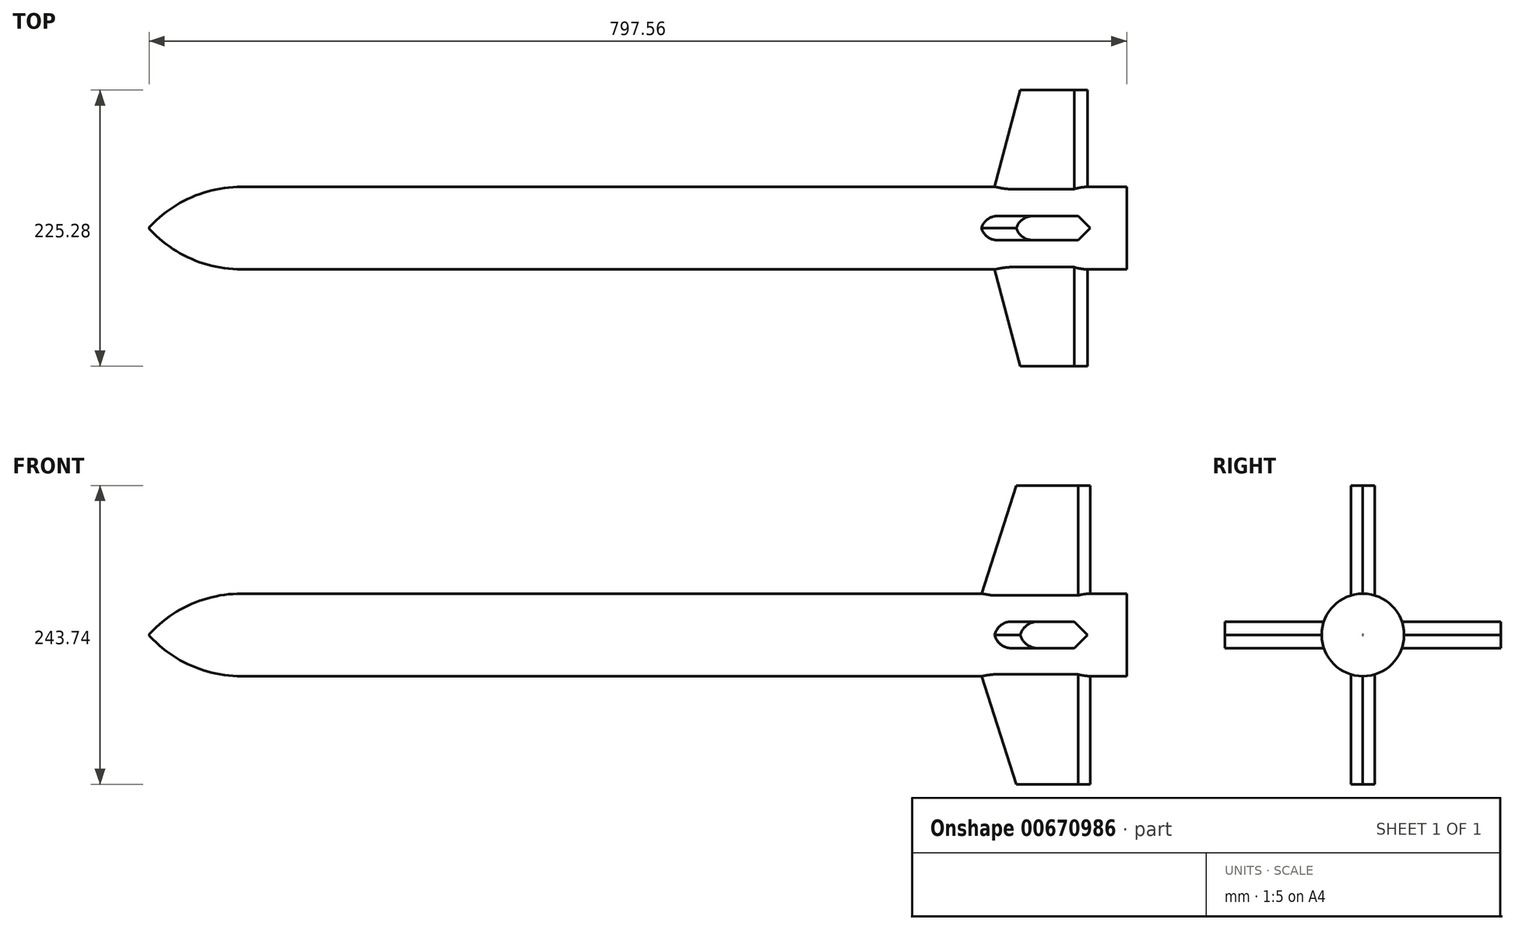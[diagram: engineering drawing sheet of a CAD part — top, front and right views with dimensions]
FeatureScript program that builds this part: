
annotation { "Feature Type Name" : "Feature", "Feature Type Description" : "" }
export const myFeature = defineFeature(function(context is Context, id is Id, definition is map)
    precondition{}
    {
        {
            var Q0;
            Q0=qCreatedBy(makeId("Right.planeOp"),FACE);
            var sketch = newSketch(context, id + "F0", { "sketchPlane" : qUnion([Q0])});
            skCircle(sketch, "E0", {"center": v(0, 0) * mm, "radius": 33.64 * mm});
            skSolve(sketch);
        }
        {
            var Q0;
            Q0 = qSketchRegion(id + "F0", true);
            extrude(context, id + "F1", {"entities" : qUnion([Q0]), "endBound" : BoundingType.SYMMETRIC, "oppositeDirection" : true, "depth" : 797.56 * mm, "offsetDistance" : 25.4 * mm});
        }
        {
            var Q0;
            Q0=makeQuery(id+"F1.opExtrude","CAP_EDGE",EDGE,{"disambiguationData":[OSD([sQuery(id+"F0.wireOp",EDGE,"E0")])],"isStart":false});
            chamfer(context, id + "F2", {"entities" : qUnion([Q0]), "width" : 33.02 * mm, "tangentPropagation" : true});
        }
        {
            var Q0;
            {var subQ0=sQuery(id+"F0.wireOp",EDGE,"E0");Q0=makeQuery(id+"F2.opChamfer","BLEND_EDGE",EDGE,{"blendedFrom":[makeQuery(id+"F1.opExtrude","CAP_EDGE",EDGE,{"disambiguationData":[OSD([subQ0])],"isStart":false}),makeQuery(id+"F1.opExtrude","SWEPT_FACE",FACE,{"disambiguationData":[OSD([subQ0])]})],"blendedInto":[makeQuery(id+"F1.opExtrude","SWEPT_FACE",FACE,{"disambiguationData":[OSD([subQ0])]})]});}
            fillet(context, id + "F3", {"entities" : qUnion([Q0]), "radius" : 101.73 * mm, "tangentPropagation" : true, "allowEdgeOverflow" : false});
        }
        {
            var Q0;
            Q0=qCreatedBy(makeId("Right.planeOp"),FACE);
            var sketch = newSketch(context, id + "F4", { "sketchPlane" : qUnion([Q0])});
            skCircle(sketch, "E1", {"center": v(0, 0) * mm, "radius": 30.05 * mm});
            skCircle(sketch, "E2", {"center": v(0, 0) * mm, "radius": 33.57 * mm});
            skSolve(sketch);
        }
        {
            var Q0;
            Q0=sQuery(id+"F4.wireOp",EDGE,"E1");
            var Q1;
            Q1=sQuery(id+"F4.wireOp",EDGE,"E2");
            extrude(context, id + "F5", {"bodyType" : ToolBodyType.SURFACE, "surfaceEntities" : qUnion([Q0, Q1]), "depth" : 431.8 * mm, "offsetDistance" : 25.4 * mm});
        }
        {
            var Q0;
            Q0=qCreatedBy(makeId("Front.planeOp"),FACE);
            var sketch = newSketch(context, id + "F6", { "sketchPlane" : qUnion([Q0])});
            skLineSegment(sketch, "E3.bottom", {"start": v(374.4, -121.87) * mm, "end": v(308.36, -121.87) * mm});
            skLineSegment(sketch, "E3.top", {"start": v(374.4, 121.87) * mm, "end": v(308.36, 121.87) * mm});
            skLineSegment(sketch, "E3.left", {"start": v(374.4, -121.87) * mm, "end": v(374.4, 121.87) * mm});
            skLineSegment(sketch, "E3.right", {"start": v(308.36, -121.87) * mm, "end": v(308.36, 121.87) * mm});
            skPoint(sketch, "E3.middle", {"position": v(341.38, 0) * mm});
            skLineSegment(sketch, "E4", {"start": v(308.36, 121.87) * mm, "end": v(269.13, 0) * mm});
            skLineSegment(sketch, "E5", {"start": v(269.13, 0) * mm, "end": v(308.36, -121.87) * mm});
            skSolve(sketch);
        }
        {
            var Q0;
            Q0 = qSketchRegion(id + "F6", true);
            extrude(context, id + "F7", {"entities" : qUnion([Q0]), "operationType" : NewBodyOperationType.ADD, "endBound" : BoundingType.SYMMETRIC, "depth" : 19.6 * mm, "offsetDistance" : 25.4 * mm});
        }
        {
            var Q0;
            Q0=makeQuery(id+"F7.opExtrude","CAP_EDGE",EDGE,{"disambiguationData":[OSD([sQuery(id+"F6.wireOp",EDGE,"E5")])],"isStart":false});
            var Q1;
            Q1=makeQuery(id+"F7.opExtrude","CAP_EDGE",EDGE,{"disambiguationData":[OSD([sQuery(id+"F6.wireOp",EDGE,"E5")])],"isStart":true});
            var Q2;
            Q2=makeQuery(id+"F7.opExtrude","CAP_EDGE",EDGE,{"disambiguationData":[OSD([sQuery(id+"F6.wireOp",EDGE,"E4")])],"isStart":false});
            var Q3;
            Q3=makeQuery(id+"F7.opExtrude","CAP_EDGE",EDGE,{"disambiguationData":[OSD([sQuery(id+"F6.wireOp",EDGE,"E4")])],"isStart":true});
            fillet(context, id + "F8", {"entities" : qUnion([Q0, Q1, Q2, Q3]), "radius" : 13.04 * mm, "tangentPropagation" : true, "allowEdgeOverflow" : false});
        }
        {
            var Q0;
            {var subQ0=sQuery(id+"F6.wireOp",EDGE,"E3.left");var subQ1=sQuery(id+"F6.wireOp",EDGE,"E3.bottom");Q0=makeQuery(id+"F7.boolean.opBoolean","SPLIT",EDGE,{"disambiguationData":[TD([makeQuery(id+"F7.opExtrude","SWEPT_FACE",FACE,{"disambiguationData":[OSD([subQ1])]})])],"derivedFrom":makeQuery(id+"F7.opExtrude","CAP_EDGE",EDGE,{"disambiguationData":[OSD([subQ0])],"isStart":false})});}
            var Q1;
            {var subQ0=sQuery(id+"F6.wireOp",EDGE,"E3.bottom");var subQ1=sQuery(id+"F6.wireOp",EDGE,"E3.left");Q1=makeQuery(id+"F7.boolean.opBoolean","SPLIT",EDGE,{"disambiguationData":[TD([makeQuery(id+"F7.opExtrude","SWEPT_FACE",FACE,{"disambiguationData":[OSD([subQ0])]})])],"derivedFrom":makeQuery(id+"F7.opExtrude","CAP_EDGE",EDGE,{"disambiguationData":[OSD([subQ1])],"isStart":true})});}
            var Q2;
            {var subQ0=sQuery(id+"F6.wireOp",EDGE,"E3.left");var subQ1=sQuery(id+"F6.wireOp",EDGE,"E3.top");Q2=makeQuery(id+"F7.boolean.opBoolean","SPLIT",EDGE,{"disambiguationData":[TD([makeQuery(id+"F7.opExtrude","SWEPT_FACE",FACE,{"disambiguationData":[OSD([subQ1])]})])],"derivedFrom":makeQuery(id+"F7.opExtrude","CAP_EDGE",EDGE,{"disambiguationData":[OSD([subQ0])],"isStart":false})});}
            var Q3;
            {var subQ0=sQuery(id+"F6.wireOp",EDGE,"E3.left");var subQ1=sQuery(id+"F6.wireOp",EDGE,"E3.top");Q3=makeQuery(id+"F7.boolean.opBoolean","SPLIT",EDGE,{"disambiguationData":[TD([makeQuery(id+"F7.opExtrude","SWEPT_FACE",FACE,{"disambiguationData":[OSD([subQ1])]})])],"derivedFrom":makeQuery(id+"F7.opExtrude","CAP_EDGE",EDGE,{"disambiguationData":[OSD([subQ0])],"isStart":true})});}
            chamfer(context, id + "F9", {"entities" : qUnion([Q0, Q1, Q2, Q3]), "width" : 15.24 * mm, "tangentPropagation" : true});
        }
        {
            var Q0;
            Q0=qCreatedBy(makeId("Top.planeOp"),FACE);
            var sketch = newSketch(context, id + "F10", { "sketchPlane" : qUnion([Q0])});
            skLineSegment(sketch, "E6.bottom", {"start": v(371.23, 112.64) * mm, "end": v(311.53, 112.64) * mm});
            skLineSegment(sketch, "E6.top", {"start": v(371.23, -112.64) * mm, "end": v(311.53, -112.64) * mm});
            skLineSegment(sketch, "E6.left", {"start": v(371.23, 112.64) * mm, "end": v(371.23, -112.64) * mm});
            skLineSegment(sketch, "E6.right", {"start": v(311.53, 112.64) * mm, "end": v(311.53, -112.64) * mm});
            skPoint(sketch, "E6.middle", {"position": v(341.38, 0) * mm});
            skLineSegment(sketch, "E7", {"start": v(311.53, 112.64) * mm, "end": v(281.68, 0) * mm});
            skLineSegment(sketch, "E8", {"start": v(281.68, 0) * mm, "end": v(311.53, -112.64) * mm});
            skSolve(sketch);
        }
        {
            var Q0;
            Q0 = qSketchRegion(id + "F10", true);
            extrude(context, id + "F11", {"entities" : qUnion([Q0]), "operationType" : NewBodyOperationType.ADD, "endBound" : BoundingType.SYMMETRIC, "depth" : 21.67 * mm, "offsetDistance" : 25.4 * mm});
        }
        {
            var Q0;
            Q0=makeQuery(id+"F11.opExtrude","CAP_EDGE",EDGE,{"disambiguationData":[OSD([sQuery(id+"F10.wireOp",EDGE,"E8")])],"isStart":false});
            var Q1;
            Q1=makeQuery(id+"F11.opExtrude","CAP_EDGE",EDGE,{"disambiguationData":[OSD([sQuery(id+"F10.wireOp",EDGE,"E8")])],"isStart":true});
            var Q2;
            Q2=makeQuery(id+"F11.opExtrude","CAP_EDGE",EDGE,{"disambiguationData":[OSD([sQuery(id+"F10.wireOp",EDGE,"E7")])],"isStart":false});
            var Q3;
            Q3=makeQuery(id+"F11.opExtrude","CAP_EDGE",EDGE,{"disambiguationData":[OSD([sQuery(id+"F10.wireOp",EDGE,"E7")])],"isStart":true});
            fillet(context, id + "F12", {"entities" : qUnion([Q0, Q1, Q2, Q3]), "radius" : 14.22 * mm, "tangentPropagation" : true, "allowEdgeOverflow" : false});
        }
        {
            var Q0;
            {var subQ0=sQuery(id+"F10.wireOp",EDGE,"E6.bottom");var subQ1=sQuery(id+"F10.wireOp",EDGE,"E6.left");Q0=makeQuery(id+"F11.boolean.opBoolean","SPLIT",EDGE,{"disambiguationData":[TD([makeQuery(id+"F11.opExtrude","SWEPT_FACE",FACE,{"disambiguationData":[OSD([subQ0])]})])],"derivedFrom":makeQuery(id+"F11.opExtrude","CAP_EDGE",EDGE,{"disambiguationData":[OSD([subQ1])],"isStart":false})});}
            var Q1;
            {var subQ0=sQuery(id+"F10.wireOp",EDGE,"E6.left");var subQ1=sQuery(id+"F10.wireOp",EDGE,"E6.bottom");Q1=makeQuery(id+"F11.boolean.opBoolean","SPLIT",EDGE,{"disambiguationData":[TD([makeQuery(id+"F11.opExtrude","SWEPT_FACE",FACE,{"disambiguationData":[OSD([subQ1])]})])],"derivedFrom":makeQuery(id+"F11.opExtrude","CAP_EDGE",EDGE,{"disambiguationData":[OSD([subQ0])],"isStart":true})});}
            var Q2;
            {var subQ0=sQuery(id+"F10.wireOp",EDGE,"E6.left");var subQ1=sQuery(id+"F10.wireOp",EDGE,"E6.top");Q2=makeQuery(id+"F11.boolean.opBoolean","SPLIT",EDGE,{"disambiguationData":[TD([makeQuery(id+"F11.opExtrude","SWEPT_FACE",FACE,{"disambiguationData":[OSD([subQ1])]})])],"derivedFrom":makeQuery(id+"F11.opExtrude","CAP_EDGE",EDGE,{"disambiguationData":[OSD([subQ0])],"isStart":false})});}
            var Q3;
            {var subQ0=sQuery(id+"F10.wireOp",EDGE,"E6.left");var subQ1=sQuery(id+"F10.wireOp",EDGE,"E6.top");Q3=makeQuery(id+"F11.boolean.opBoolean","SPLIT",EDGE,{"disambiguationData":[TD([makeQuery(id+"F11.opExtrude","SWEPT_FACE",FACE,{"disambiguationData":[OSD([subQ1])]})])],"derivedFrom":makeQuery(id+"F11.opExtrude","CAP_EDGE",EDGE,{"disambiguationData":[OSD([subQ0])],"isStart":true})});}
            chamfer(context, id + "F13", {"entities" : qUnion([Q0, Q1, Q2, Q3]), "width" : 15.24 * mm, "tangentPropagation" : true});
        }
    });
